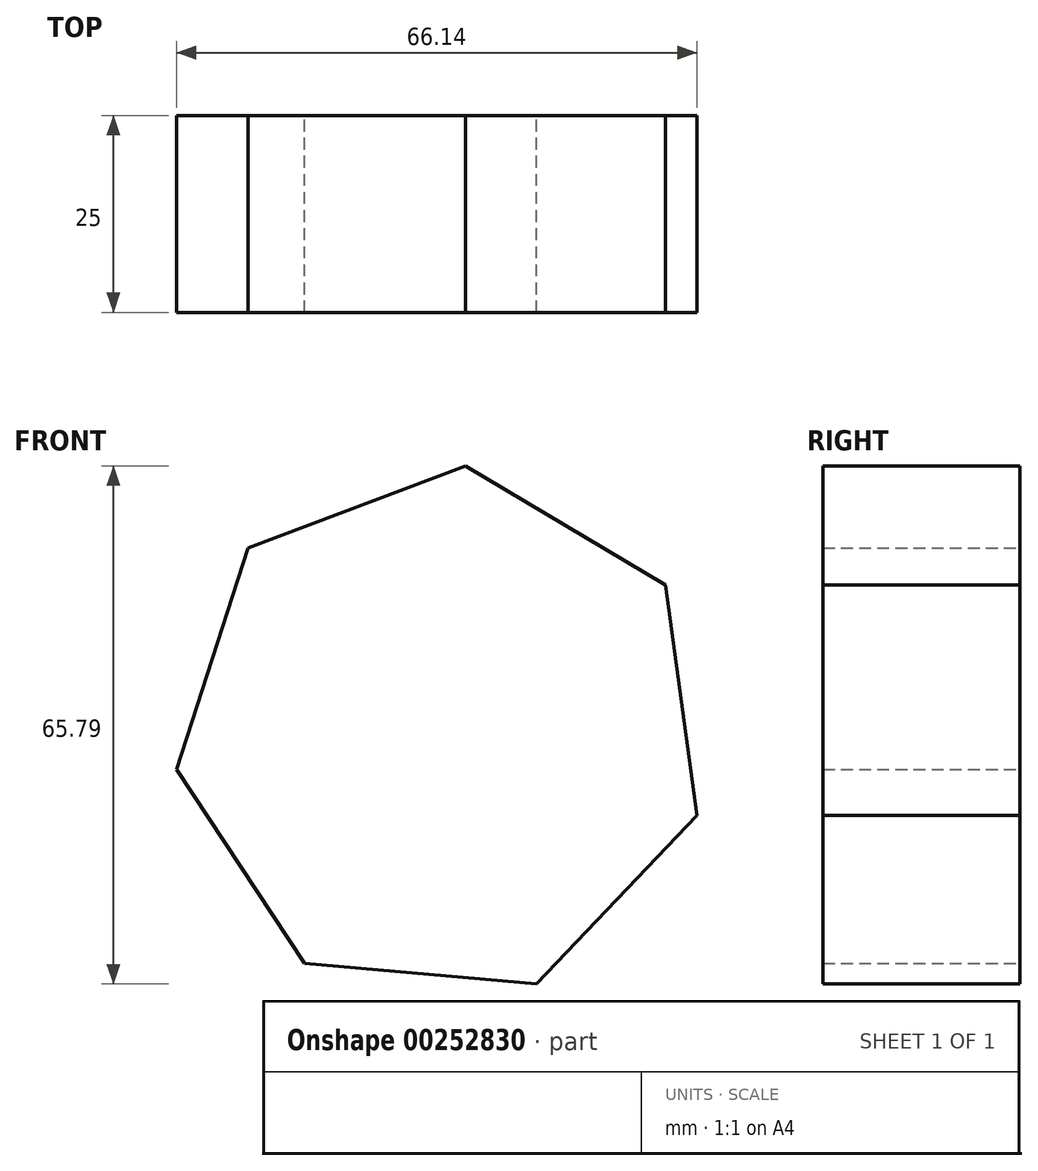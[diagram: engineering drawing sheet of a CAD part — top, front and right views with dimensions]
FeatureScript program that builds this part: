
annotation { "Feature Type Name" : "Feature", "Feature Type Description" : "" }
export const myFeature = defineFeature(function(context is Context, id is Id, definition is map)
    precondition{}
    {
        {
            var Q0;
            Q0=qCreatedBy(makeId("Front.planeOp"),FACE);
            var sketch = newSketch(context, id + "F0", { "sketchPlane" : qUnion([Q0])});
            skCircle(sketch, "E0.cCircle", {"center": v(0, 0) * mm, "radius": 34.06 * mm, "construction": true});
            skLineSegment(sketch, "E0.0", {"start": v(28.4, 18.8) * mm, "end": v(32.4, -10.49) * mm});
            skLineSegment(sketch, "E0.1", {"start": v(32.4, -10.49) * mm, "end": v(12, -31.87) * mm});
            skLineSegment(sketch, "E0.2", {"start": v(12, -31.87) * mm, "end": v(-17.44, -29.25) * mm});
            skLineSegment(sketch, "E0.3", {"start": v(-17.44, -29.25) * mm, "end": v(-33.74, -4.6) * mm});
            skLineSegment(sketch, "E0.4", {"start": v(-33.74, -4.6) * mm, "end": v(-24.64, 23.5) * mm});
            skLineSegment(sketch, "E0.5", {"start": v(-24.64, 23.5) * mm, "end": v(3.02, 33.92) * mm});
            skLineSegment(sketch, "E0.6", {"start": v(3.02, 33.92) * mm, "end": v(28.4, 18.8) * mm});
            skSolve(sketch);
        }
        {
            var Q0;
            Q0=makeQuery(id+"F0.imprint","IMPRINT",FACE,{"disambiguationData":[TD([[makeQuery(id+"F0.imprint","IMPRINT",EDGE,{"derivedFrom":sQuery(id+"F0.wireOp",EDGE,"E0.0")}),-1.0]])]});
            extrude(context, id + "F1", {"entities" : qUnion([Q0]), "endBound" : BoundingType.SYMMETRIC, "depth" : 25 * mm});
        }
    });
